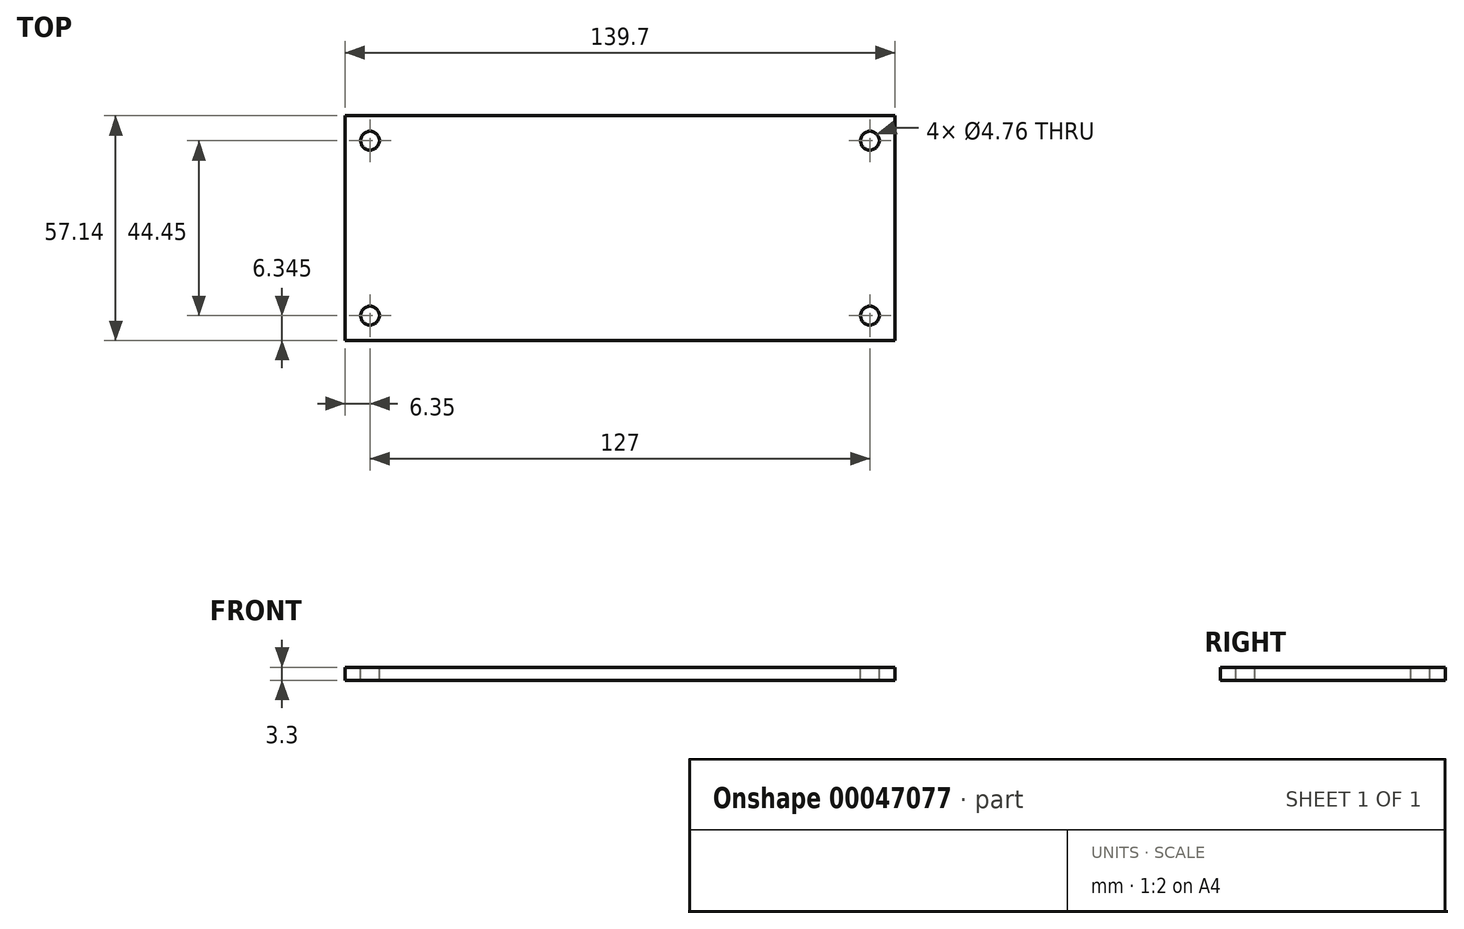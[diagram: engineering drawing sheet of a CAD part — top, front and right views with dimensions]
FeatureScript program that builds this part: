
annotation { "Feature Type Name" : "Feature", "Feature Type Description" : "" }
export const myFeature = defineFeature(function(context is Context, id is Id, definition is map)
    precondition{}
    {
        {
            var Q0;
            Q0=qCreatedBy(makeId("Top.planeOp"),FACE);
            var sketch = newSketch(context, id + "F0", { "sketchPlane" : qUnion([Q0])});
            skLineSegment(sketch, "E0.rect.bottom", {"start": v(69.85, 28.57) * mm, "end": v(-69.85, 28.57) * mm});
            skLineSegment(sketch, "E0.rect.top", {"start": v(69.85, -28.58) * mm, "end": v(-69.85, -28.58) * mm});
            skLineSegment(sketch, "E0.rect.left", {"start": v(69.85, 28.58) * mm, "end": v(69.85, -28.58) * mm});
            skLineSegment(sketch, "E0.rect.right", {"start": v(-69.85, 28.58) * mm, "end": v(-69.85, -28.58) * mm});
            skPoint(sketch, "E0.rect.middle", {"position": v(0, 0) * mm});
            skSolve(sketch);
        }
        {
            var Q0;
            Q0 = qSketchRegion(id + "F0", true);
            extrude(context, id + "F1", {"entities" : qUnion([Q0]), "endBound" : BoundingType.SYMMETRIC, "depth" : 3.3 * mm});
        }
        {
            var Q0;
            Q0=makeQuery(id+"F1.opExtrude","CAP_FACE",FACE,{"disambiguationData":[OSD([sQuery(id+"F0.wireOp",EDGE,"E0.rect.bottom"),sQuery(id+"F0.wireOp",EDGE,"E0.rect.top"),sQuery(id+"F0.wireOp",EDGE,"E0.rect.left"),sQuery(id+"F0.wireOp",EDGE,"E0.rect.right")])],"isStart":false});
            var sketch = newSketch(context, id + "F2", { "sketchPlane" : qUnion([Q0])});
            skCircle(sketch, "E1", {"center": v(-63.5, -22.23) * mm, "radius": 2.38 * mm});
            skCircle(sketch, "E2.MirrorC", {"center": v(-63.5, 22.23) * mm, "radius": 2.38 * mm});
            skCircle(sketch, "E3.MirrorC", {"center": v(63.5, -22.23) * mm, "radius": 2.38 * mm});
            skCircle(sketch, "E4.MirrorC", {"center": v(63.5, 22.23) * mm, "radius": 2.38 * mm});
            skSolve(sketch);
        }
        {
            var Q0;
            Q0 = qSketchRegion(id + "F2", true);
            extrude(context, id + "F3", {"entities" : qUnion([Q0]), "operationType" : NewBodyOperationType.REMOVE, "endBound" : BoundingType.UP_TO_NEXT, "oppositeDirection" : true, "depth" : 25.4 * mm});
        }
    });
